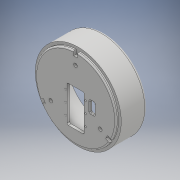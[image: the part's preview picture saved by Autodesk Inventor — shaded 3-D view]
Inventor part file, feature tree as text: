
AUTODESK INVENTOR PART (.ipt)
format: ipt  version: 2018 (Build 220112000, 112)  size: 540,160 bytes
history: native  units: mm
features: extrude x5, sketch x4, fillet x3, pattern_circular x2, hole x1, projected_geometry x1
ambient origin geometry x8: Origin, YZ Plane, XZ Plane, XY Plane, X Axis, Y Axis, Z Axis, Center Point
bodies: Solid1 (feature_tree)
feature tree (16):
  sketch  "Sketch1"  dims[d0=122.0mm d1=10.0mm]
  extrude  "Extrusion1"  Depth=10.0mm
  extrude  "Extrusion2"  Depth=4.0mm
  extrude  "Extrusion3"  Depth=35.5mm TaperAngle=0.0deg
  extrude  "Extrusion5"  Depth=2.0mm TaperAngle=0.0deg
  pattern_circular  "Circular Pattern1"  Count=4  [1 undecoded]
  extrude  "Extrusion6"  Depth=6.0mm
  fillet  "Fillet2"  Radius=10.0mm
  fillet  "Fillet3"  Radius=30.0mm
  fillet  "Fillet4"  Radius=6.0mm
  hole  "Hole1"  [1 undecoded]
  pattern_circular  "Circular Pattern2"  [2 undecoded]
  sketch  "Sketch2"  dims[d2=4.0mm d3=26.0mm]
  projected_geometry  "Projected Loop1"
  sketch  "Sketch3"  dims[d4=55.0mm d5=35.5mm d6=0.0mm]
  sketch  "Sketch7"  dims[d7=4.0mm d8=0.0mm d9=39.5mm d10=0.0mm d14=40.0mm d15=6.0mm d16=10.0mm d17=0.0mm d18=30.0mm d19=360.0deg d21=6.0mm d22=15.0mm d23=9.0mm d24=40.8mm d25=10.0mm d26=0.0mm d27=1.0mm d28=2.0mm d29=4.0mm d33=11.0mm d34=5.5mm d35=6.0mm d36=4.0mm d37=2.0mm d38=90.0deg d39=8.0mm d40=20.594885mm d41=30.0mm d42=360.0deg]
note: 4 required parameter values undecoded (feature->parameter linkage not recoverable at this tier; creation-order binding heuristic only, values carry confidence <= 0.55)
